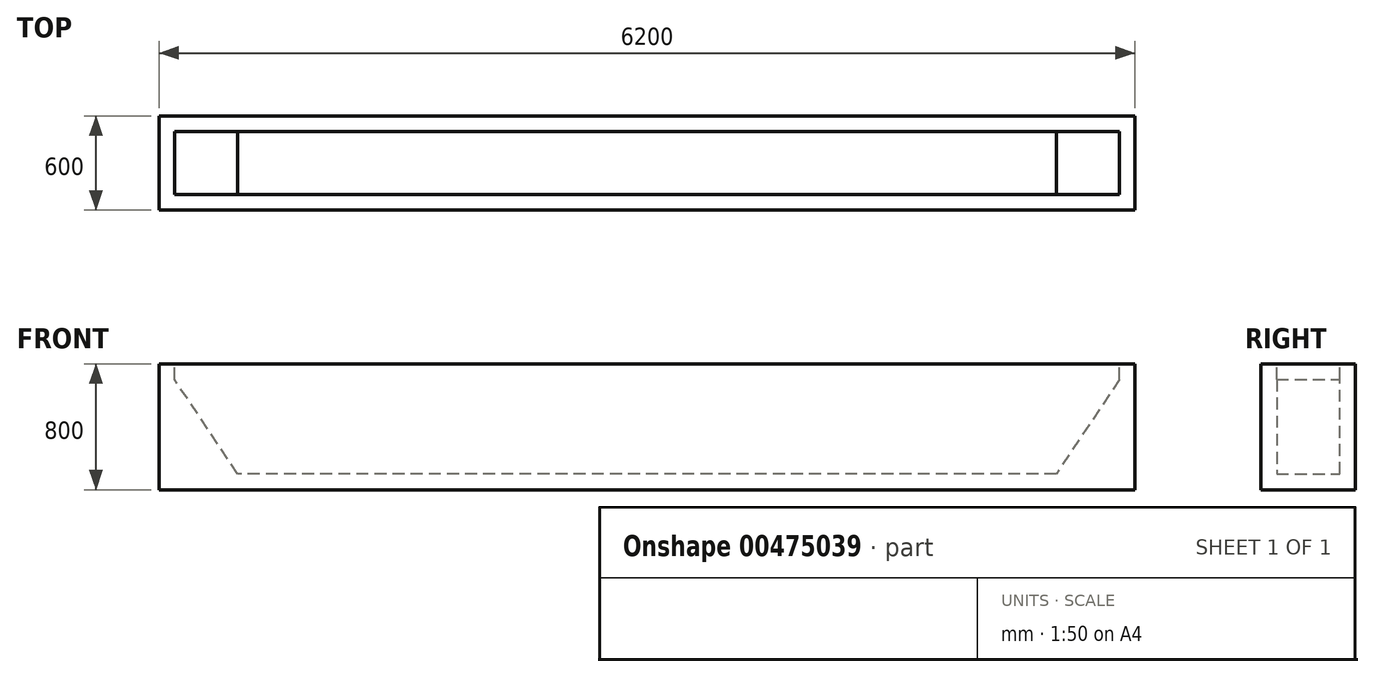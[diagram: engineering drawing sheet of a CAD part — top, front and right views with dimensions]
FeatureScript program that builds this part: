
annotation { "Feature Type Name" : "Feature", "Feature Type Description" : "" }
export const myFeature = defineFeature(function(context is Context, id is Id, definition is map)
    precondition{}
    {
        {
            var Q0;
            Q0=qCreatedBy(makeId("Front.planeOp"),FACE);
            var sketch = newSketch(context, id + "F0", { "sketchPlane" : qUnion([Q0])});
            skLineSegment(sketch, "E0.bottom", {"start": v(3100, -400) * mm, "end": v(-3100, -400) * mm});
            skLineSegment(sketch, "E0.top", {"start": v(3100, 400) * mm, "end": v(-3100, 400) * mm});
            skLineSegment(sketch, "E0.left", {"start": v(3100, -400) * mm, "end": v(3100, 400) * mm});
            skLineSegment(sketch, "E0.right", {"start": v(-3100, -400) * mm, "end": v(-3100, 400) * mm});
            skPoint(sketch, "E0.middle", {"position": v(0, 0) * mm});
            skSolve(sketch);
        }
        {
            var Q0;
            Q0=makeQuery(id+"F0.imprint","IMPRINT",FACE,{"disambiguationData":[TD([[makeQuery(id+"F0.imprint","IMPRINT",EDGE,{"derivedFrom":sQuery(id+"F0.wireOp",EDGE,"E0.bottom")}),-1.0]])]});
            extrude(context, id + "F1", {"entities" : qUnion([Q0]), "endBound" : BoundingType.SYMMETRIC, "depth" : 600 * mm});
        }
        {
            var Q0;
            Q0=makeQuery(id+"F1.opExtrude","SWEPT_FACE",FACE,{"disambiguationData":[OSD([sQuery(id+"F0.wireOp",EDGE,"E0.top")])]});
            var sketch = newSketch(context, id + "F2", { "sketchPlane" : qUnion([Q0])});
            skLineSegment(sketch, "E1.bottom", {"start": v(3000, 200) * mm, "end": v(-3000, 200) * mm});
            skLineSegment(sketch, "E1.top", {"start": v(3000, -200) * mm, "end": v(-3000, -200) * mm});
            skLineSegment(sketch, "E1.left", {"start": v(3000, 200) * mm, "end": v(3000, -200) * mm});
            skLineSegment(sketch, "E1.right", {"start": v(-3000, 200) * mm, "end": v(-3000, -200) * mm});
            skPoint(sketch, "E1.middle", {"position": v(0, 0) * mm});
            skSolve(sketch);
        }
        {
            var Q0;
            Q0=makeQuery(id+"F2.imprint","IMPRINT",FACE,{"disambiguationData":[TD([[makeQuery(id+"F2.imprint","IMPRINT",EDGE,{"derivedFrom":sQuery(id+"F2.wireOp",EDGE,"E1.bottom")}),1.0]])]});
            extrude(context, id + "F3", {"entities" : qUnion([Q0]), "operationType" : NewBodyOperationType.REMOVE, "oppositeDirection" : true, "depth" : 700 * mm});
        }
        {
            var Q0;
            Q0=makeQuery(id+"F3.boolean.opBoolean","COPY",FACE,{"derivedFrom":makeQuery(id+"F3.opExtrude","SWEPT_FACE",FACE,{"disambiguationData":[OSD([sQuery(id+"F2.wireOp",EDGE,"E1.bottom")])]})});
            var sketch = newSketch(context, id + "F4", { "sketchPlane" : qUnion([Q0])});
            skLineSegment(sketch, "E2", {"start": v(-3000, 300) * mm, "end": v(-2600, -300) * mm});
            skSolve(sketch);
        }
        {
            var Q0;
            {var subQ0=sQuery(id+"F4.wireOp",EDGE,"E2");Q0=makeQuery(id+"F4.imprint","IMPRINT",FACE,{"disambiguationData":[TD([[makeQuery(id+"F4.imprint","IMPRINT",EDGE,{"derivedFrom":subQ0}),-1.0]])]});}
            extrude(context, id + "F5", {"entities" : qUnion([Q0]), "operationType" : NewBodyOperationType.ADD, "endBound" : BoundingType.UP_TO_NEXT, "depth" : 385 * mm});
        }
        {
            var Q0;
            Q0=makeQuery(id+"F3.boolean.opBoolean","COPY",FACE,{"derivedFrom":makeQuery(id+"F3.opExtrude","SWEPT_FACE",FACE,{"disambiguationData":[OSD([sQuery(id+"F2.wireOp",EDGE,"E1.bottom")])]})});
            var sketch = newSketch(context, id + "F6", { "sketchPlane" : qUnion([Q0])});
            skLineSegment(sketch, "E3", {"start": v(2600, -300) * mm, "end": v(3000, 300) * mm});
            skSolve(sketch);
        }
        {
            var Q0;
            {var subQ0=sQuery(id+"F6.wireOp",EDGE,"E3");Q0=makeQuery(id+"F6.imprint","IMPRINT",FACE,{"disambiguationData":[TD([[makeQuery(id+"F6.imprint","IMPRINT",EDGE,{"derivedFrom":subQ0}),-1.0]])]});}
            extrude(context, id + "F7", {"entities" : qUnion([Q0]), "operationType" : NewBodyOperationType.ADD, "endBound" : BoundingType.UP_TO_NEXT, "depth" : 25 * mm});
        }
    });
